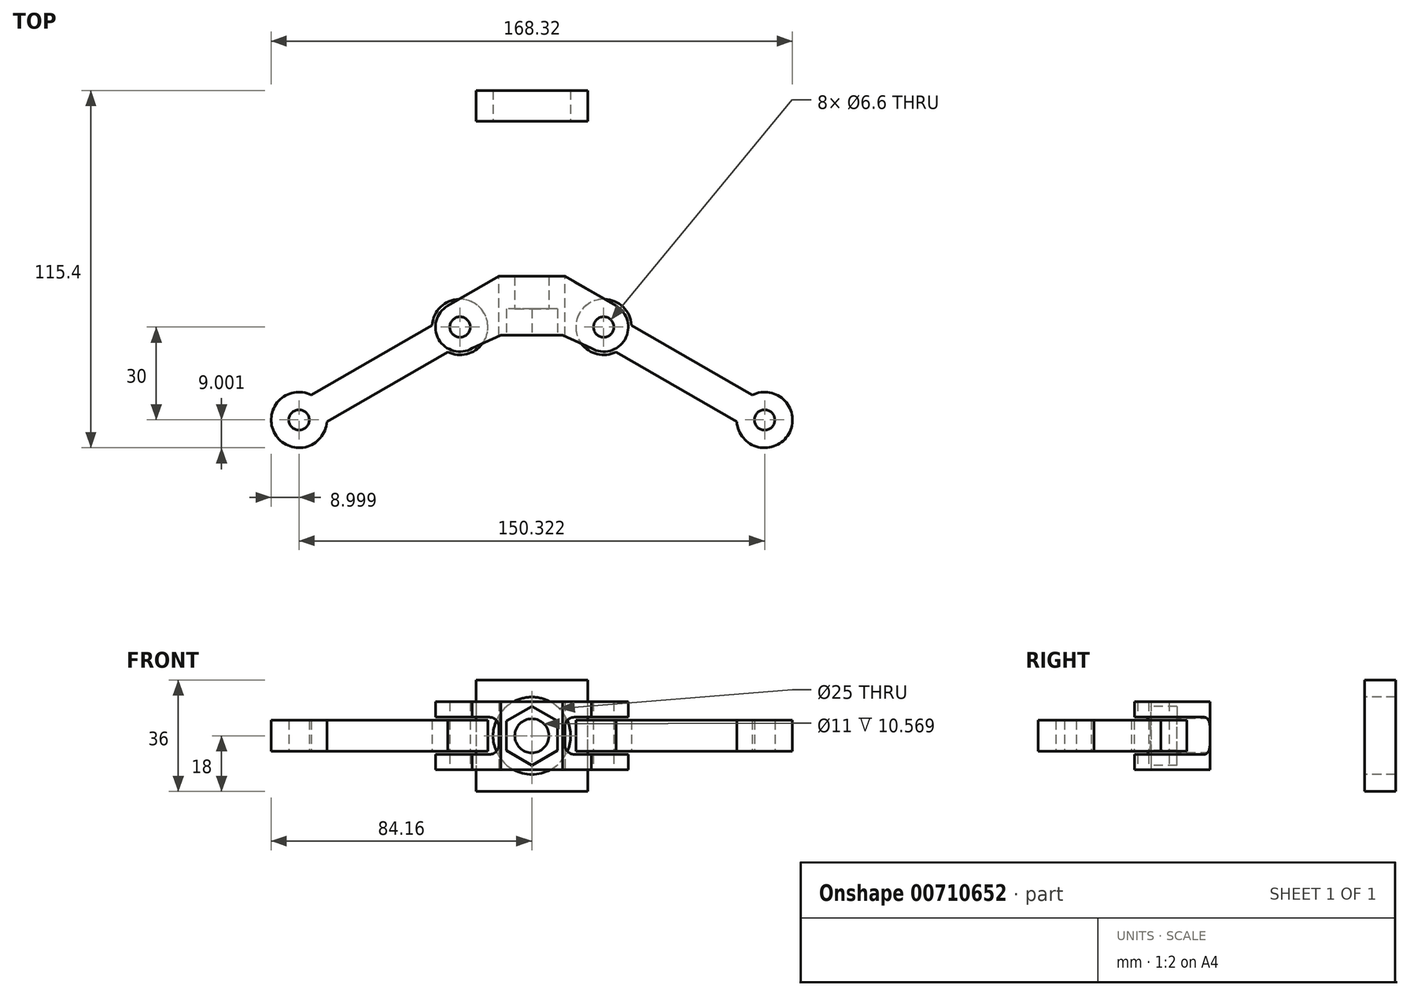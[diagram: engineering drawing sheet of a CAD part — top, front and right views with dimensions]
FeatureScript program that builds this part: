
annotation { "Feature Type Name" : "Feature", "Feature Type Description" : "" }
export const myFeature = defineFeature(function(context is Context, id is Id, definition is map)
    precondition{}
    {
        {
            var Q0;
            Q0=qCreatedBy(makeId("Top.planeOp"),FACE);
            var sketch = newSketch(context, id + "F0", { "sketchPlane" : qUnion([Q0])});
            skLineSegment(sketch, "E0", {"start": v(0, 0) * mm, "end": v(0, -59.92) * mm, "construction": true});
            skLineSegment(sketch, "E1", {"start": v(0, 0) * mm, "end": v(10.67, 0) * mm});
            skLineSegment(sketch, "E2", {"start": v(10.67, 0) * mm, "end": v(27.17, -9.53) * mm});
            skLineSegment(sketch, "E3", {"start": v(27.17, -9.53) * mm, "end": v(19.23, -23.27) * mm, "construction": true});
            skLineSegment(sketch, "E4", {"start": v(19.23, -23.27) * mm, "end": v(10, -18.97) * mm});
            skLineSegment(sketch, "E5", {"start": v(10, -18.97) * mm, "end": v(0, -18.97) * mm});
            skArc(sketch, "E6", {"start": v(19.23, -23.27) * mm, "mid": v(30.07, -20.37) * mm, "end": v(27.17, -9.52) * mm});
            skCircle(sketch, "E7", {"center": v(23.2, -16.4) * mm, "radius": 3.3 * mm});
            skLineSegment(sketch, "E8.MirrorCS", {"start": v(-10, -18.97) * mm, "end": v(0, -18.97) * mm});
            skLineSegment(sketch, "E9.MirrorCS", {"start": v(-19.23, -23.27) * mm, "end": v(-10, -18.97) * mm});
            skArc(sketch, "E10.MirrorCS", {"start": v(-19.23, -23.27) * mm, "mid": v(-30.07, -20.37) * mm, "end": v(-27.17, -9.52) * mm});
            skLineSegment(sketch, "E11.MirrorCS", {"start": v(-10.67, 0) * mm, "end": v(-27.17, -9.53) * mm});
            skLineSegment(sketch, "E12.MirrorCS", {"start": v(0, 0) * mm, "end": v(-10.67, 0) * mm});
            skCircle(sketch, "E13.MirrorC", {"center": v(-23.2, -16.4) * mm, "radius": 3.3 * mm});
            skSolve(sketch);
        }
        {
            var Q0;
            Q0=makeQuery(id+"F0.imprint","IMPRINT",FACE,{"disambiguationData":[TD([[makeQuery(id+"F0.imprint","IMPRINT",EDGE,{"derivedFrom":sQuery(id+"F0.wireOp",EDGE,"E1")}),-1.0]])]});
            extrude(context, id + "F1", {"entities" : qUnion([Q0]), "depth" : 22 * mm, "offsetDistance" : 25.4 * mm});
        }
        {
            var Q0;
            Q0=makeQuery(id+"F1.opExtrude","SWEPT_FACE",FACE,{"disambiguationData":[OSD([sQuery(id+"F0.wireOp",EDGE,"E5"),sQuery(id+"F0.wireOp",EDGE,"E8.MirrorCS")])]});
            var sketch = newSketch(context, id + "F2", { "sketchPlane" : qUnion([Q0])});
            skLineSegment(sketch, "E14", {"start": v(0, 22) * mm, "end": v(0, 0) * mm, "construction": true});
            skCircle(sketch, "E15", {"center": v(0, 11) * mm, "radius": 5.5 * mm});
            skSolve(sketch);
        }
        {
            var Q0;
            Q0=makeQuery(id+"F2.imprint","IMPRINT",FACE,{"disambiguationData":[TD([[makeQuery(id+"F2.imprint","IMPRINT",EDGE,{"derivedFrom":sQuery(id+"F2.wireOp",EDGE,"E15")}),1.0]])]});
            extrude(context, id + "F3", {"entities" : qUnion([Q0]), "operationType" : NewBodyOperationType.REMOVE, "endBound" : BoundingType.THROUGH_ALL, "oppositeDirection" : true, "depth" : 25 * mm, "offsetDistance" : 25 * mm});
        }
        {
            var Q0;
            Q0=makeQuery(id+"F1.opExtrude","SWEPT_FACE",FACE,{"disambiguationData":[OSD([sQuery(id+"F0.wireOp",EDGE,"E5"),sQuery(id+"F0.wireOp",EDGE,"E8.MirrorCS")])]});
            var sketch = newSketch(context, id + "F4", { "sketchPlane" : qUnion([Q0])});
            skLineSegment(sketch, "E16", {"start": v(0, 22) * mm, "end": v(0, 0) * mm, "construction": true});
            skCircle(sketch, "E17.cCircle", {"center": v(0, 11) * mm, "radius": 8.25 * mm, "construction": true});
            skLineSegment(sketch, "E17.0", {"start": v(-8.25, 6.24) * mm, "end": v(-8.25, 15.76) * mm});
            skLineSegment(sketch, "E17.1", {"start": v(-8.25, 15.76) * mm, "end": v(0, 20.53) * mm});
            skLineSegment(sketch, "E17.2", {"start": v(0, 20.53) * mm, "end": v(8.25, 15.76) * mm});
            skLineSegment(sketch, "E17.3", {"start": v(8.25, 15.76) * mm, "end": v(8.25, 6.24) * mm});
            skLineSegment(sketch, "E17.4", {"start": v(8.25, 6.24) * mm, "end": v(0, 1.47) * mm});
            skLineSegment(sketch, "E17.5", {"start": v(0, 1.47) * mm, "end": v(-8.25, 6.24) * mm});
            skPoint(sketch, "E17.0.midPoint", {"position": v(-8.25, 11) * mm});
            skSolve(sketch);
        }
        {
            var Q0;
            Q0=makeQuery(id+"F4.imprint","IMPRINT",FACE,{"disambiguationData":[TD([[makeQuery(id+"F4.imprint","IMPRINT",EDGE,{"derivedFrom":sQuery(id+"F4.wireOp",EDGE,"E17.0")}),-1.0]])]});
            extrude(context, id + "F5", {"entities" : qUnion([Q0]), "operationType" : NewBodyOperationType.REMOVE, "oppositeDirection" : true, "depth" : 8.4 * mm, "offsetDistance" : 25 * mm});
        }
        {
            var Q0;
            Q0=makeQuery(id+"F1.opExtrude","SWEPT_FACE",FACE,{"disambiguationData":[OSD([sQuery(id+"F0.wireOp",EDGE,"E1"),sQuery(id+"F0.wireOp",EDGE,"E12.MirrorCS")])]});
            var sketch = newSketch(context, id + "F6", { "sketchPlane" : qUnion([Q0])});
            skLineSegment(sketch, "E18", {"start": v(0, 22) * mm, "end": v(0, 0) * mm, "construction": true});
            skLineSegment(sketch, "E19", {"start": v(-10.67, 17) * mm, "end": v(-40.6, 17) * mm});
            skLineSegment(sketch, "E20", {"start": v(-40.6, 17) * mm, "end": v(-40.6, 5) * mm});
            skLineSegment(sketch, "E21", {"start": v(-40.6, 5) * mm, "end": v(-10.67, 5) * mm});
            skLineSegment(sketch, "E22.MirrorCS", {"start": v(10.67, 17) * mm, "end": v(40.6, 17) * mm});
            skLineSegment(sketch, "E23.MirrorCS", {"start": v(40.6, 17) * mm, "end": v(40.6, 5) * mm});
            skLineSegment(sketch, "E24.MirrorCS", {"start": v(40.6, 5) * mm, "end": v(10.67, 5) * mm});
            skLineSegment(sketch, "E25", {"start": v(-10.67, 11) * mm, "end": v(10.67, 11) * mm, "construction": true});
            skSolve(sketch);
        }
        {
            var Q0;
            {var subQ0=sQuery(id+"F6.wireOp",EDGE,"E19");Q0=makeQuery(id+"F6.imprint","IMPRINT",FACE,{"disambiguationData":[TD([[makeQuery(id+"F6.imprint","IMPRINT",EDGE,{"derivedFrom":subQ0}),1.0]])]});}
            var Q1;
            {var subQ0=sQuery(id+"F6.wireOp",EDGE,"E22.MirrorCS");Q1=makeQuery(id+"F6.imprint","IMPRINT",FACE,{"disambiguationData":[TD([[makeQuery(id+"F6.imprint","IMPRINT",EDGE,{"derivedFrom":subQ0}),-1.0]])]});}
            extrude(context, id + "F7", {"entities" : qUnion([Q0, Q1]), "operationType" : NewBodyOperationType.REMOVE, "endBound" : BoundingType.THROUGH_ALL, "oppositeDirection" : true, "depth" : 25 * mm, "offsetDistance" : 25 * mm});
        }
        {
            var Q0;
            Q0=makeQuery(id+"F7.boolean.opBoolean","COPY",EDGE,{"derivedFrom":makeQuery(id+"F7.opExtrude","SWEPT_EDGE",EDGE,{"disambiguationData":[OSD([sQuery(id+"F0.wireOp",EDGE,"E1"),sQuery(id+"F0.wireOp",EDGE,"E2"),sQuery(id+"F6.wireOp",EDGE,"E21")])]})});
            var Q1;
            Q1=makeQuery(id+"F7.boolean.opBoolean","COPY",EDGE,{"derivedFrom":makeQuery(id+"F7.opExtrude","SWEPT_EDGE",EDGE,{"disambiguationData":[OSD([sQuery(id+"F0.wireOp",EDGE,"E1"),sQuery(id+"F0.wireOp",EDGE,"E2"),sQuery(id+"F6.wireOp",EDGE,"E19")])]})});
            var Q2;
            Q2=makeQuery(id+"F7.boolean.opBoolean","COPY",EDGE,{"derivedFrom":makeQuery(id+"F7.opExtrude","SWEPT_EDGE",EDGE,{"disambiguationData":[OSD([sQuery(id+"F0.wireOp",EDGE,"E11.MirrorCS"),sQuery(id+"F0.wireOp",EDGE,"E12.MirrorCS"),sQuery(id+"F6.wireOp",EDGE,"E22.MirrorCS")])]})});
            var Q3;
            Q3=makeQuery(id+"F7.boolean.opBoolean","COPY",EDGE,{"derivedFrom":makeQuery(id+"F7.opExtrude","SWEPT_EDGE",EDGE,{"disambiguationData":[OSD([sQuery(id+"F0.wireOp",EDGE,"E11.MirrorCS"),sQuery(id+"F0.wireOp",EDGE,"E12.MirrorCS"),sQuery(id+"F6.wireOp",EDGE,"E24.MirrorCS")])]})});
            fillet(context, id + "F8", {"entities" : qUnion([Q0, Q1, Q2, Q3]), "radius" : 3 * mm, "tangentPropagation" : true, "allowEdgeOverflow" : false});
        }
        {
            var Q0;
            Q0=makeQuery(id+"F7.boolean.opBoolean","COPY",FACE,{"derivedFrom":makeQuery(id+"F7.opExtrude","SWEPT_FACE",FACE,{"disambiguationData":[OSD([sQuery(id+"F6.wireOp",EDGE,"E21")])]})});
            cPlane(context, id + "F9", {"entities" : qUnion([Q0]), "cplaneType" : CPlaneType.OFFSET, "offset" : 1 * mm, "width" : 150 * mm, "height" : 150 * mm});
        }
        {
            var Q0;
            Q0=qCreatedBy(id+"F9.planeOp",FACE);
            var sketch = newSketch(context, id + "F10", { "sketchPlane" : qUnion([Q0])});
            skCircle(sketch, "E26.0", {"center": v(23.2, -16.4) * mm, "radius": 3.3 * mm});
            skArc(sketch, "E27", {"start": v(32.18, -15.81) * mm, "mid": v(15.4, -11.9) * mm, "end": v(27.18, -24.47) * mm});
            skLineSegment(sketch, "E28", {"start": v(23.2, -16.4) * mm, "end": v(23.2, -62.8) * mm, "construction": true});
            skLineSegment(sketch, "E29", {"start": v(23.2, -16.4) * mm, "end": v(63.21, -39.5) * mm, "construction": true});
            skLineSegment(sketch, "E30", {"start": v(27.18, -24.47) * mm, "end": v(66.18, -46.99) * mm});
            skLineSegment(sketch, "E31.MirrorCS", {"start": v(32.18, -15.81) * mm, "end": v(71.18, -38.33) * mm});
            skLineSegment(sketch, "E32", {"start": v(51.68, -27.07) * mm, "end": v(46.68, -35.73) * mm, "construction": true});
            skArc(sketch, "E33.MirrorC", {"start": v(71.18, -38.33) * mm, "mid": v(82.96, -50.9) * mm, "end": v(66.18, -46.99) * mm});
            skCircle(sketch, "E34.MirrorC", {"center": v(75.16, -46.4) * mm, "radius": 3.3 * mm});
            skSolve(sketch);
        }
        {
            var Q0;
            Q0=makeQuery(id+"F10.imprint","IMPRINT",FACE,{"disambiguationData":[TD([[makeQuery(id+"F10.imprint","IMPRINT",EDGE,{"derivedFrom":sQuery(id+"F10.wireOp",EDGE,"E26.0")}),-1.0]])]});
            extrude(context, id + "F11", {"entities" : qUnion([Q0]), "depth" : 10 * mm, "offsetDistance" : 25 * mm});
        }
        {
            var Q0;
            Q0=makeQuery(id+"F11.opExtrude","SWEPT_BODY",BODY,{"disambiguationData":[OSD([sQuery(id+"F10.wireOp",EDGE,"E26.0"),sQuery(id+"F10.wireOp",EDGE,"E27"),sQuery(id+"F10.wireOp",EDGE,"E30"),sQuery(id+"F10.wireOp",EDGE,"E31.MirrorCS"),sQuery(id+"F10.wireOp",EDGE,"E33.MirrorC"),sQuery(id+"F10.wireOp",EDGE,"E34.MirrorC")])]});
            var Q1;
            Q1=qCreatedBy(makeId("Right.planeOp"),FACE);
            mirror(context, id + "F12", {"entities" : qUnion([Q0]), "mirrorPlane" : qUnion([Q1])});
        }
        {
            var Q0;
            Q0=makeQuery(id+"F1.opExtrude","SWEPT_FACE",FACE,{"disambiguationData":[OSD([sQuery(id+"F0.wireOp",EDGE,"E1"),sQuery(id+"F0.wireOp",EDGE,"E12.MirrorCS")])]});
            cPlane(context, id + "F13", {"entities" : qUnion([Q0]), "cplaneType" : CPlaneType.OFFSET, "offset" : 50 * mm, "width" : 150 * mm, "height" : 150 * mm});
        }
        {
            var Q0;
            Q0=qCreatedBy(id+"F13.planeOp",FACE);
            var sketch = newSketch(context, id + "F14", { "sketchPlane" : qUnion([Q0])});
            skCircle(sketch, "E35.0", {"center": v(0, 11) * mm, "radius": 5.5 * mm});
            skCircle(sketch, "E36", {"center": v(0, 11) * mm, "radius": 12.5 * mm});
            skLineSegment(sketch, "E37", {"start": v(-18, 29) * mm, "end": v(18, 29) * mm});
            skLineSegment(sketch, "E38", {"start": v(18, 29) * mm, "end": v(18, -7) * mm});
            skLineSegment(sketch, "E39", {"start": v(18, -7) * mm, "end": v(-18, -7) * mm});
            skLineSegment(sketch, "E40", {"start": v(-18, -7) * mm, "end": v(-18, 29) * mm});
            skLineSegment(sketch, "E41", {"start": v(0, 11) * mm, "end": v(0, 43.95) * mm, "construction": true});
            skLineSegment(sketch, "E42", {"start": v(0, 11) * mm, "end": v(41.1, 11) * mm, "construction": true});
            skSolve(sketch);
        }
        {
            var Q0;
            Q0=makeQuery(id+"F14.imprint","IMPRINT",FACE,{"disambiguationData":[TD([[makeQuery(id+"F14.imprint","IMPRINT",EDGE,{"derivedFrom":sQuery(id+"F14.wireOp",EDGE,"E36")}),-1.0]])]});
            extrude(context, id + "F15", {"entities" : qUnion([Q0]), "depth" : 10 * mm, "offsetDistance" : 25 * mm});
        }
    });
